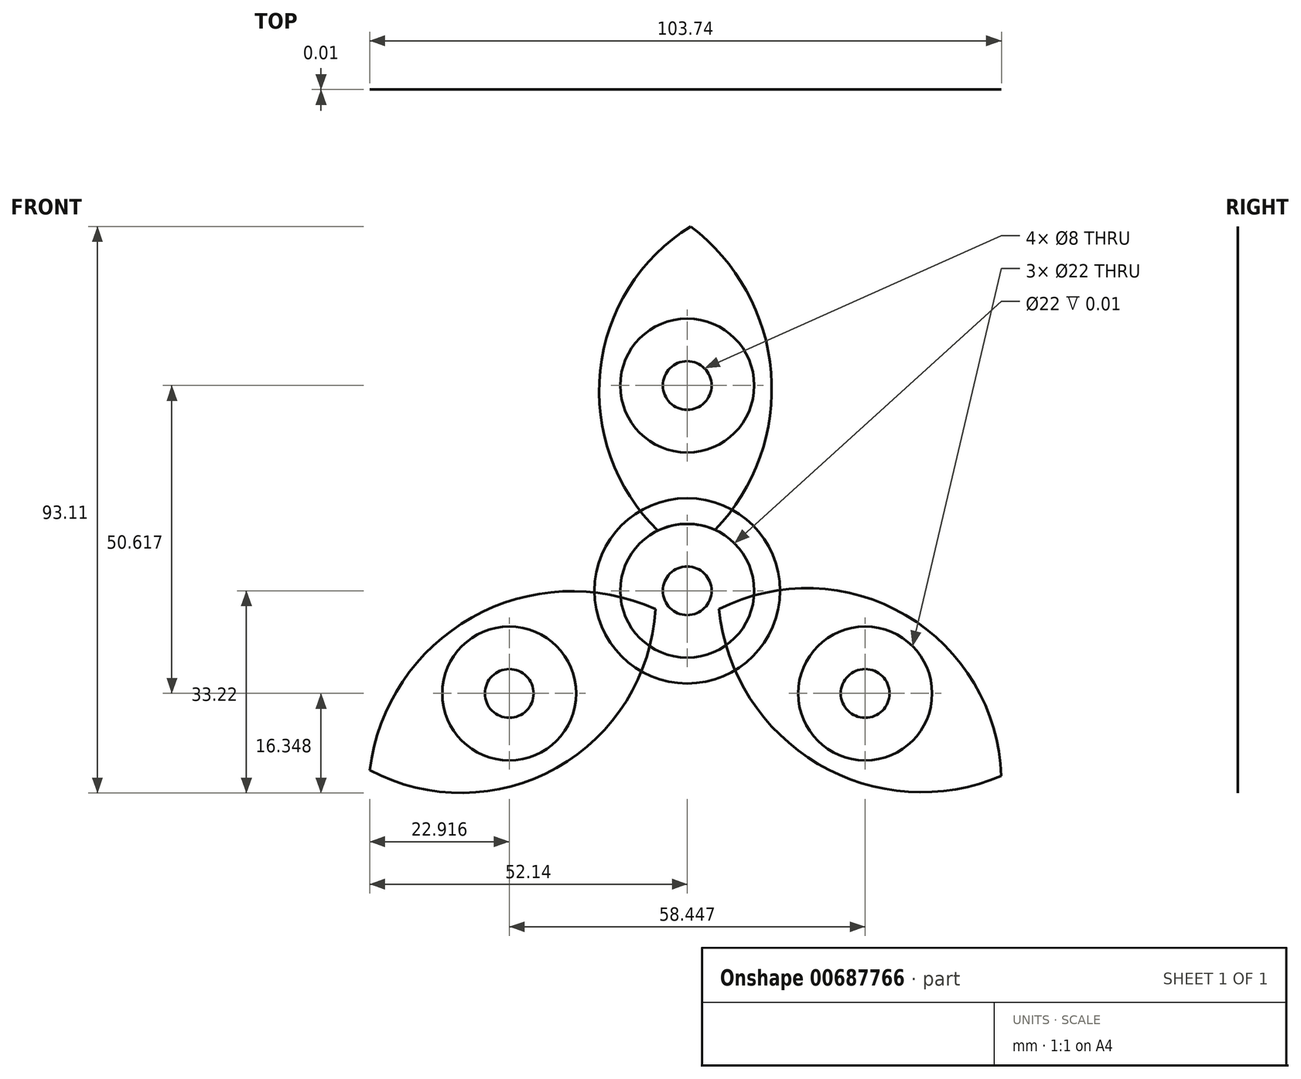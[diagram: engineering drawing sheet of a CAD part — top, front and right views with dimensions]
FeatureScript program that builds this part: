
annotation { "Feature Type Name" : "Feature", "Feature Type Description" : "" }
export const myFeature = defineFeature(function(context is Context, id is Id, definition is map)
    precondition{}
    {
        {
            assignVariable(context, id + "F0", {"name" : "th", "anyValue" : 1 / 101.6 * mm});
        }
        {
            var Q0;
            Q0=qCreatedBy(makeId("Front.planeOp"),FACE);
            var sketch = newSketch(context, id + "F1", { "sketchPlane" : qUnion([Q0])});
            skCircle(sketch, "E0", {"center": v(0, 0) * mm, "radius": 15.24 * mm});
            skSolve(sketch);
        }
        {
            var Q0;
            Q0 = qSketchRegion(id + "F1", true);
            extrude(context, id + "F2", {"entities" : qUnion([Q0]), "depth" : getVariable(context, 'th'), "offsetDistance" : 25.4 * mm});
        }
        {
            var Q0;
            Q0=makeQuery(id+"F2.opExtrude","CAP_FACE",FACE,{"disambiguationData":[OSD([sQuery(id+"F1.wireOp",EDGE,"E0")])],"isStart":false});
            var sketch = newSketch(context, id + "F3", { "sketchPlane" : qUnion([Q0])});
            skCircle(sketch, "E1", {"center": v(0, 0) * mm, "radius": 4 * mm});
            skCircle(sketch, "E2", {"center": v(0, 0) * mm, "radius": 11 * mm});
            skSolve(sketch);
        }
        {
            var Q0;
            Q0=makeQuery(id+"F3.imprint","IMPRINT",FACE,{"disambiguationData":[TD([[makeQuery(id+"F3.imprint","IMPRINT",EDGE,{"derivedFrom":sQuery(id+"F3.wireOp",EDGE,"E1")}),1.0]])]});
            var Q1;
            Q1=makeQuery(id+"F3.imprint","IMPRINT",FACE,{"disambiguationData":[TD([[makeQuery(id+"F3.imprint","IMPRINT",EDGE,{"derivedFrom":sQuery(id+"F3.wireOp",EDGE,"E1")}),-1.0]])]});
            extrude(context, id + "F4", {"entities" : qUnion([Q0, Q1]), "operationType" : NewBodyOperationType.REMOVE, "endBound" : BoundingType.THROUGH_ALL, "oppositeDirection" : true, "depth" : getVariable(context, 'th'), "offsetDistance" : 25.4 * mm});
        }
        {
            var Q0;
            Q0=qCreatedBy(makeId("Front.planeOp"),FACE);
            var sketch = newSketch(context, id + "F5", { "sketchPlane" : qUnion([Q0])});
            skCircle(sketch, "E3", {"center": v(0, 0) * mm, "radius": 63.5 * mm, "construction": true});
            skArc(sketch, "E4", {"start": v(0, 6.03) * mm, "mid": v(13.89, 32.82) * mm, "end": v(0.54, 59.9) * mm});
            skArc(sketch, "E5", {"start": v(0.54, 59.9) * mm, "mid": v(-14.48, 33.1) * mm, "end": v(0, 6.03) * mm});
            skCircle(sketch, "E6", {"center": v(0, 33.74) * mm, "radius": 4 * mm});
            skCircle(sketch, "E7", {"center": v(0, 33.74) * mm, "radius": 11 * mm});
            skSolve(sketch);
        }
        {
            var Q0;
            Q0 = qSketchRegion(id + "F3", true);
            extrude(context, id + "F6", {"entities" : qUnion([Q0]), "oppositeDirection" : true, "depth" : getVariable(context, 'th'), "offsetDistance" : 25.4 * mm});
        }
        {
            var Q0;
            Q0=makeQuery(id+"F5.imprint","IMPRINT",FACE,{"disambiguationData":[TD([[makeQuery(id+"F5.imprint","IMPRINT",EDGE,{"derivedFrom":sQuery(id+"F5.wireOp",EDGE,"bQhvghNw-zhm9-qtSo-MyOr-sX3rV5HjiShR")}),1.0]])]});
            var Q1;
            Q1=makeQuery(id+"F5.imprint","IMPRINT",FACE,{"disambiguationData":[TD([[makeQuery(id+"F5.imprint","IMPRINT",EDGE,{"derivedFrom":sQuery(id+"F5.wireOp",EDGE,"E4")}),1.0]])]});
            extrude(context, id + "F7", {"entities" : qUnion([Q0, Q1]), "depth" : getVariable(context, 'th'), "offsetDistance" : 25.4 * mm});
        }
        {
            var Q0;
            Q0=makeQuery(id+"F5.imprint","IMPRINT",FACE,{"disambiguationData":[TD([[makeQuery(id+"F5.imprint","IMPRINT",EDGE,{"derivedFrom":sQuery(id+"F5.wireOp",EDGE,"E6")}),-1.0]])]});
            extrude(context, id + "F8", {"entities" : qUnion([Q0]), "depth" : getVariable(context, 'th'), "offsetDistance" : 25.4 * mm});
        }
        {
            var Q0;
            Q0=makeQuery(id+"F8.opExtrude","SWEPT_BODY",BODY,{"disambiguationData":[OSD([sQuery(id+"F5.wireOp",EDGE,"E6"),sQuery(id+"F5.wireOp",EDGE,"E7")])]});
            var Q1;
            Q1=makeQuery(id+"F7.opExtrude","SWEPT_BODY",BODY,{"disambiguationData":[OSD([sQuery(id+"F5.wireOp",EDGE,"E4"),sQuery(id+"F5.wireOp",EDGE,"E5"),sQuery(id+"F5.wireOp",EDGE,"E7")])]});
            var Q2;
            Q2=makeQuery(id+"F6.opExtrude","CAP_EDGE",EDGE,{"disambiguationData":[OSD([sQuery(id+"F3.wireOp",EDGE,"E1")])],"isStart":false});
            circularPattern(context, id + "F9", {"entities" : qUnion([Q0, Q1]), "axis" : qUnion([Q2]), "angle" : 360 * degree, "instanceCount" : 3, "equalSpace" : true});
        }
        {
            var Q0;
            Q0=makeQuery(id+"F6.opExtrude","SWEPT_BODY",BODY,{"disambiguationData":[OSD([sQuery(id+"F3.wireOp",EDGE,"E1"),sQuery(id+"F3.wireOp",EDGE,"E2")])]});
            var Q1;
            Q1=makeQuery(id+"F7.opExtrude","SWEPT_BODY",BODY,{"disambiguationData":[OSD([sQuery(id+"F5.wireOp",EDGE,"E4"),sQuery(id+"F5.wireOp",EDGE,"E5"),sQuery(id+"F5.wireOp",EDGE,"E7")])]});
            booleanBodies(context, id + "F10", {"operationType" : BooleanOperationType.SUBTRACTION, "tools" : qUnion([Q0]), "targets" : qUnion([Q1]), "keepTools" : true});
        }
    });
